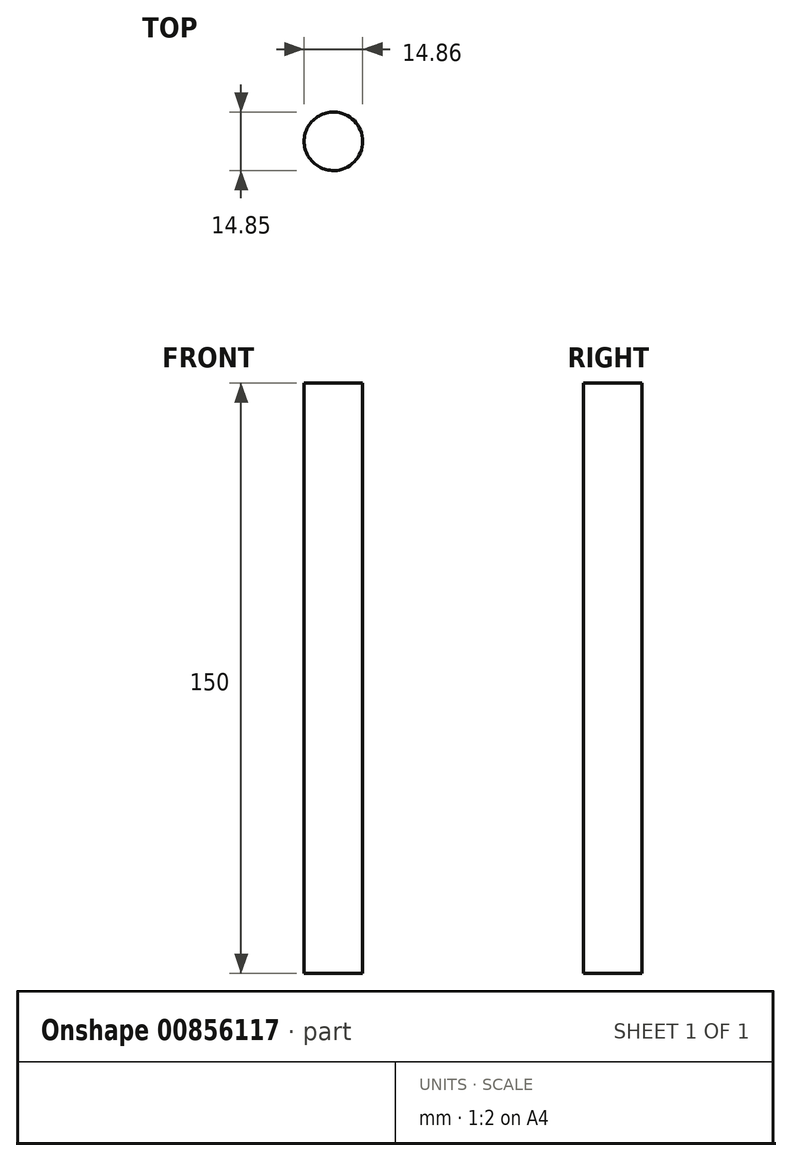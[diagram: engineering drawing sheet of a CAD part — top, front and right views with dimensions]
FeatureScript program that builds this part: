
annotation { "Feature Type Name" : "Feature", "Feature Type Description" : "" }
export const myFeature = defineFeature(function(context is Context, id is Id, definition is map)
    precondition{}
    {
        {
            var Q0;
            Q0=qCreatedBy(makeId("Top.planeOp"),FACE);
            var sketch = newSketch(context, id + "F0", { "sketchPlane" : qUnion([Q0])});
            skArc(sketch, "E0", {"start": v(0, 0) * mm, "mid": v(7.32, 7.43) * mm, "end": v(0, 14.85) * mm});
            skArc(sketch, "E1", {"start": v(0, 14.85) * mm, "mid": v(-7.54, 7.43) * mm, "end": v(0, 0) * mm});
            skSolve(sketch);
        }
        {
            var Q0;
            Q0=makeQuery(id+"F0.imprint","IMPRINT",FACE,{"disambiguationData":[TD([[makeQuery(id+"F0.imprint","IMPRINT",EDGE,{"derivedFrom":sQuery(id+"F0.wireOp",EDGE,"E0")}),1.0]])]});
            extrude(context, id + "F1", {"entities" : qUnion([Q0]), "depth" : 150 * mm, "offsetDistance" : 25 * mm});
        }
    });
